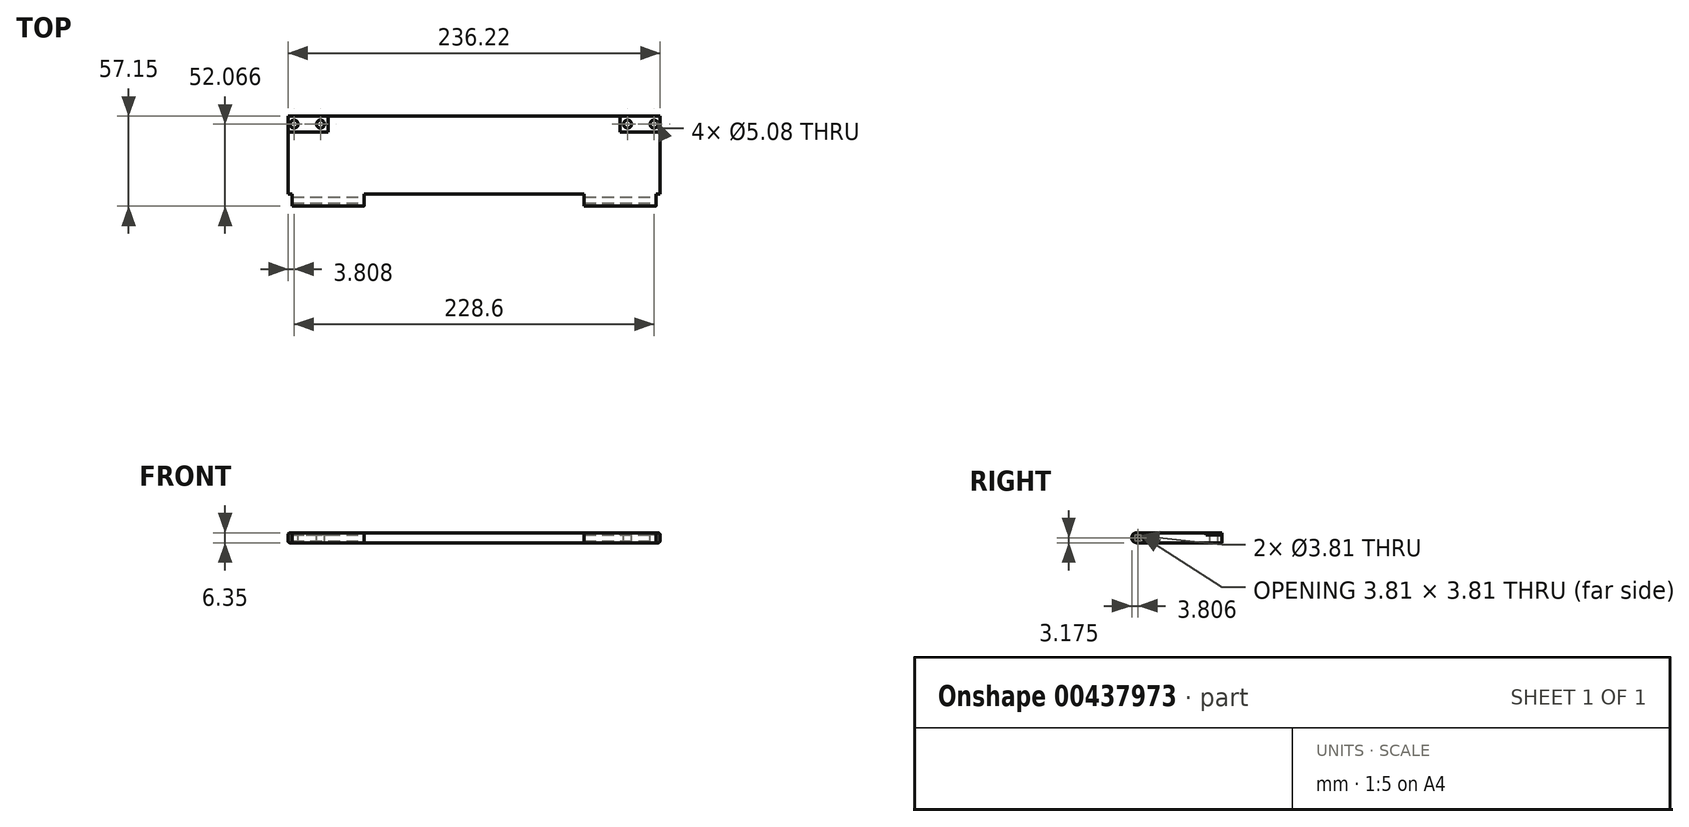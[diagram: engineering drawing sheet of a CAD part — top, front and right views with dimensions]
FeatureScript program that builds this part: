
annotation { "Feature Type Name" : "Feature", "Feature Type Description" : "" }
export const myFeature = defineFeature(function(context is Context, id is Id, definition is map)
    precondition{}
    {
        {
            var Q0;
            Q0=qCreatedBy(makeId("Top.planeOp"),FACE);
            var sketch = newSketch(context, id + "F0", { "sketchPlane" : qUnion([Q0])});
            skLineSegment(sketch, "E0.bottom", {"start": v(-101.64, -2.08) * mm, "end": v(-53.38, -2.08) * mm});
            skLineSegment(sketch, "E0.left", {"start": v(-101.64, -2.08) * mm, "end": v(-101.64, -51.61) * mm});
            skLineSegment(sketch, "E0.right", {"start": v(134.58, -2.08) * mm, "end": v(134.58, -51.61) * mm});
            skLineSegment(sketch, "E1.left", {"start": v(-53.38, -51.61) * mm, "end": v(-53.38, -59.23) * mm});
            skPoint(sketch, "E2.oppositeSnap0", {"position": v(86.32, -66.98) * mm});
            skLineSegment(sketch, "E2.top", {"start": v(-53.38, -2.08) * mm, "end": v(86.32, -2.08) * mm});
            skLineSegment(sketch, "E2.left", {"start": v(-53.38, -2.08) * mm, "end": v(-53.38, -2.08) * mm});
            skLineSegment(sketch, "E2.right", {"start": v(86.32, -2.08) * mm, "end": v(86.32, -2.08) * mm});
            skLineSegment(sketch, "E3.trimOffspring", {"start": v(86.32, -2.08) * mm, "end": v(134.58, -2.08) * mm});
            skLineSegment(sketch, "E4.top", {"start": v(-101.64, -59.23) * mm, "end": v(-53.38, -59.23) * mm});
            skLineSegment(sketch, "E4.left", {"start": v(-101.64, -51.61) * mm, "end": v(-101.64, -59.23) * mm});
            skLineSegment(sketch, "E5.bottom", {"start": v(86.32, -59.23) * mm, "end": v(134.58, -59.23) * mm});
            skLineSegment(sketch, "E5.right", {"start": v(134.58, -59.23) * mm, "end": v(134.58, -51.61) * mm});
            skLineSegment(sketch, "E6", {"start": v(-53.38, -51.61) * mm, "end": v(86.32, -51.61) * mm});
            skLineSegment(sketch, "E7", {"start": v(86.32, -59.23) * mm, "end": v(86.32, -51.61) * mm});
            skSolve(sketch);
        }
        {
            var Q0;
            Q0=qSketchRegion(id+"F0",true);
            extrude(context, id + "F1", {"entities" : qUnion([Q0]), "depth" : 6.35 * mm});
        }
        {
            var Q0;
            Q0=makeQuery(id+"F1.opExtrude","CAP_FACE",FACE,{"disambiguationData":[OSD([sQuery(id+"F0.wireOp",EDGE,"E0.bottom"),sQuery(id+"F0.wireOp",EDGE,"E0.top"),sQuery(id+"F0.wireOp",EDGE,"E0.left"),sQuery(id+"F0.wireOp",EDGE,"E0.right"),sQuery(id+"F0.wireOp",EDGE,"E1.top"),sQuery(id+"F0.wireOp",EDGE,"E1.left"),sQuery(id+"F0.wireOp",EDGE,"E1.right"),sQuery(id+"F0.wireOp",EDGE,"E2.top"),sQuery(id+"F0.wireOp",EDGE,"E3.trimOffspring"),sQuery(id+"F0.wireOp",EDGE,"966923a9-03d6-48e2-8a9f-226ebbd281b2.trimOffspring")])],"isStart":false});
            var sketch = newSketch(context, id + "F2", { "sketchPlane" : qUnion([Q0])});
            skLineSegment(sketch, "E8.bottom", {"start": v(-101.64, -2.08) * mm, "end": v(-76.24, -2.08) * mm});
            skLineSegment(sketch, "E8.top", {"start": v(-101.64, -12.24) * mm, "end": v(-76.24, -12.24) * mm});
            skLineSegment(sketch, "E8.left", {"start": v(-101.64, -2.08) * mm, "end": v(-101.64, -12.24) * mm});
            skLineSegment(sketch, "E8.right", {"start": v(-76.24, -2.08) * mm, "end": v(-76.24, -12.24) * mm});
            skLineSegment(sketch, "E9.bottom", {"start": v(134.58, -2.08) * mm, "end": v(109.18, -2.08) * mm});
            skLineSegment(sketch, "E9.top", {"start": v(134.58, -12.24) * mm, "end": v(109.18, -12.24) * mm});
            skLineSegment(sketch, "E9.left", {"start": v(134.58, -2.08) * mm, "end": v(134.58, -12.24) * mm});
            skLineSegment(sketch, "E9.right", {"start": v(109.18, -2.08) * mm, "end": v(109.18, -12.24) * mm});
            skSolve(sketch);
        }
        {
            var Q0;
            Q0=qSketchRegion(id+"F2",true);
            extrude(context, id + "F3", {"entities" : qUnion([Q0]), "operationType" : NewBodyOperationType.REMOVE, "oppositeDirection" : true, "depth" : 1.27 * mm});
        }
        {
            var Q0;
            Q0=makeQuery(id+"F3.boolean.opBoolean","COPY",FACE,{"derivedFrom":makeQuery(id+"F3.opExtrude","CAP_FACE",FACE,{"disambiguationData":[OSD([sQuery(id+"F2.wireOp",EDGE,"E8.bottom"),sQuery(id+"F2.wireOp",EDGE,"E8.top"),sQuery(id+"F2.wireOp",EDGE,"E8.left"),sQuery(id+"F2.wireOp",EDGE,"E8.right")])],"isStart":false})});
            var sketch = newSketch(context, id + "F4", { "sketchPlane" : qUnion([Q0])});
            skCircle(sketch, "E10", {"center": v(-97.83, -7.16) * mm, "radius": 2.54 * mm});
            skPoint(sketch, "E10.centerSnap0", {"position": v(-101.64, -7.16) * mm});
            skCircle(sketch, "E11", {"center": v(-81.07, -7.16) * mm, "radius": 2.54 * mm});
            skSolve(sketch);
        }
        {
            var Q0;
            Q0=qSketchRegion(id+"F4",true);
            extrude(context, id + "F5", {"entities" : qUnion([Q0]), "operationType" : NewBodyOperationType.REMOVE, "oppositeDirection" : true, "depth" : 25.4 * mm});
        }
        {
            var Q0;
            Q0=makeQuery(id+"F3.boolean.opBoolean","COPY",FACE,{"derivedFrom":makeQuery(id+"F3.opExtrude","CAP_FACE",FACE,{"disambiguationData":[OSD([sQuery(id+"F2.wireOp",EDGE,"E9.bottom"),sQuery(id+"F2.wireOp",EDGE,"E9.top"),sQuery(id+"F2.wireOp",EDGE,"E9.left"),sQuery(id+"F2.wireOp",EDGE,"E9.right")])],"isStart":false})});
            var sketch = newSketch(context, id + "F6", { "sketchPlane" : qUnion([Q0])});
            skCircle(sketch, "E12", {"center": v(130.77, -7.16) * mm, "radius": 2.54 * mm});
            skPoint(sketch, "E12.centerSnap0", {"position": v(134.58, -7.16) * mm});
            skCircle(sketch, "E13", {"center": v(114, -7.16) * mm, "radius": 2.54 * mm});
            skSolve(sketch);
        }
        {
            var Q0;
            Q0=qSketchRegion(id+"F6",true);
            extrude(context, id + "F7", {"entities" : qUnion([Q0]), "operationType" : NewBodyOperationType.REMOVE, "oppositeDirection" : true, "depth" : 25.4 * mm});
        }
        {
            var Q0;
            Q0=makeQuery(id+"F1.opExtrude","SWEPT_FACE",FACE,{"disambiguationData":[OSD([sQuery(id+"F0.wireOp",EDGE,"E1.left")])]});
            var sketch = newSketch(context, id + "F8", { "sketchPlane" : qUnion([Q0])});
            skCircle(sketch, "E14", {"center": v(-55.42, 3.18) * mm, "radius": 1.9 * mm});
            skPoint(sketch, "E14.centerSnap0", {"position": v(-55.42, 6.35) * mm});
            skPoint(sketch, "E14.centerSnap1", {"position": v(-59.23, 3.18) * mm});
            skSolve(sketch);
        }
        {
            var Q0;
            Q0=qSketchRegion(id+"F8",true);
            extrude(context, id + "F9", {"entities" : qUnion([Q0]), "operationType" : NewBodyOperationType.REMOVE, "oppositeDirection" : true, "depth" : 508 * mm, "symmetric" : true});
        }
        {
            var Q0;
            Q0=makeQuery(id+"F1.opExtrude","CAP_EDGE",EDGE,{"disambiguationData":[OSD([sQuery(id+"F0.wireOp",EDGE,"E4.top")])],"isStart":false});
            var Q1;
            Q1=makeQuery(id+"F1.opExtrude","CAP_EDGE",EDGE,{"disambiguationData":[OSD([sQuery(id+"F0.wireOp",EDGE,"E4.top")])],"isStart":true});
            var Q2;
            Q2=makeQuery(id+"F1.opExtrude","CAP_EDGE",EDGE,{"disambiguationData":[OSD([sQuery(id+"F0.wireOp",EDGE,"E5.bottom")])],"isStart":false});
            var Q3;
            Q3=makeQuery(id+"F1.opExtrude","CAP_EDGE",EDGE,{"disambiguationData":[OSD([sQuery(id+"F0.wireOp",EDGE,"E5.bottom")])],"isStart":true});
            fillet(context, id + "F10", {"entities" : qUnion([Q0, Q1, Q2, Q3]), "radius" : 3.17 * mm, "tangentPropagation" : true, "allowEdgeOverflow" : false});
        }
        {
            var Q0;
            Q0=makeQuery(id+"F1.opExtrude","CAP_EDGE",EDGE,{"disambiguationData":[OSD([sQuery(id+"F0.wireOp",EDGE,"E0.left"),sQuery(id+"F0.wireOp",EDGE,"E4.left")])],"isStart":false});
            var Q1;
            Q1=makeQuery(id+"F1.opExtrude","CAP_EDGE",EDGE,{"disambiguationData":[OSD([sQuery(id+"F0.wireOp",EDGE,"E0.right"),sQuery(id+"F0.wireOp",EDGE,"E5.right")])],"isStart":false});
            fillet(context, id + "F11", {"entities" : qUnion([Q0, Q1]), "radius" : 1.27 * mm, "tangentPropagation" : true, "allowEdgeOverflow" : false});
        }
        {
            var Q0;
            Q0=makeQuery(id+"F11.opFillet","SPLIT",FACE,{"disambiguationData":[OD(0.0)],"derivedFrom":makeQuery(id+"F1.opExtrude","SWEPT_FACE",FACE,{"disambiguationData":[OSD([sQuery(id+"F0.wireOp",EDGE,"E0.left"),sQuery(id+"F0.wireOp",EDGE,"E4.left")])]})});
            var sketch = newSketch(context, id + "F12", { "sketchPlane" : qUnion([Q0])});
            skLineSegment(sketch, "E15.bottom", {"start": v(51.61, 8.56) * mm, "end": v(62.33, 8.56) * mm});
            skLineSegment(sketch, "E15.top", {"start": v(51.61, -2.8) * mm, "end": v(62.33, -2.8) * mm});
            skLineSegment(sketch, "E15.left", {"start": v(51.61, 8.56) * mm, "end": v(51.61, -2.8) * mm});
            skLineSegment(sketch, "E15.right", {"start": v(62.33, 8.56) * mm, "end": v(62.33, -2.8) * mm});
            skSolve(sketch);
        }
        {
            var Q0;
            Q0=qSketchRegion(id+"F12",true);
            extrude(context, id + "F13", {"entities" : qUnion([Q0]), "operationType" : NewBodyOperationType.REMOVE, "oppositeDirection" : true, "depth" : 2.54 * mm});
        }
        {
            var Q0;
            Q0=makeQuery(id+"F11.opFillet","SPLIT",FACE,{"disambiguationData":[OD(0.0)],"derivedFrom":makeQuery(id+"F1.opExtrude","SWEPT_FACE",FACE,{"disambiguationData":[OSD([sQuery(id+"F0.wireOp",EDGE,"E0.right"),sQuery(id+"F0.wireOp",EDGE,"E5.right")])]})});
            var sketch = newSketch(context, id + "F14", { "sketchPlane" : qUnion([Q0])});
            skLineSegment(sketch, "E16.bottom", {"start": v(-59.43, 6.53) * mm, "end": v(-51.61, 6.53) * mm});
            skLineSegment(sketch, "E16.top", {"start": v(-59.43, -0.54) * mm, "end": v(-51.61, -0.54) * mm});
            skLineSegment(sketch, "E16.left", {"start": v(-59.43, 6.53) * mm, "end": v(-59.43, -0.54) * mm});
            skLineSegment(sketch, "E16.right", {"start": v(-51.61, 6.53) * mm, "end": v(-51.61, -0.54) * mm});
            skSolve(sketch);
        }
        {
            var Q0;
            Q0=qSketchRegion(id+"F14",true);
            extrude(context, id + "F15", {"entities" : qUnion([Q0]), "operationType" : NewBodyOperationType.REMOVE, "oppositeDirection" : true, "depth" : 2.54 * mm});
        }
    });
